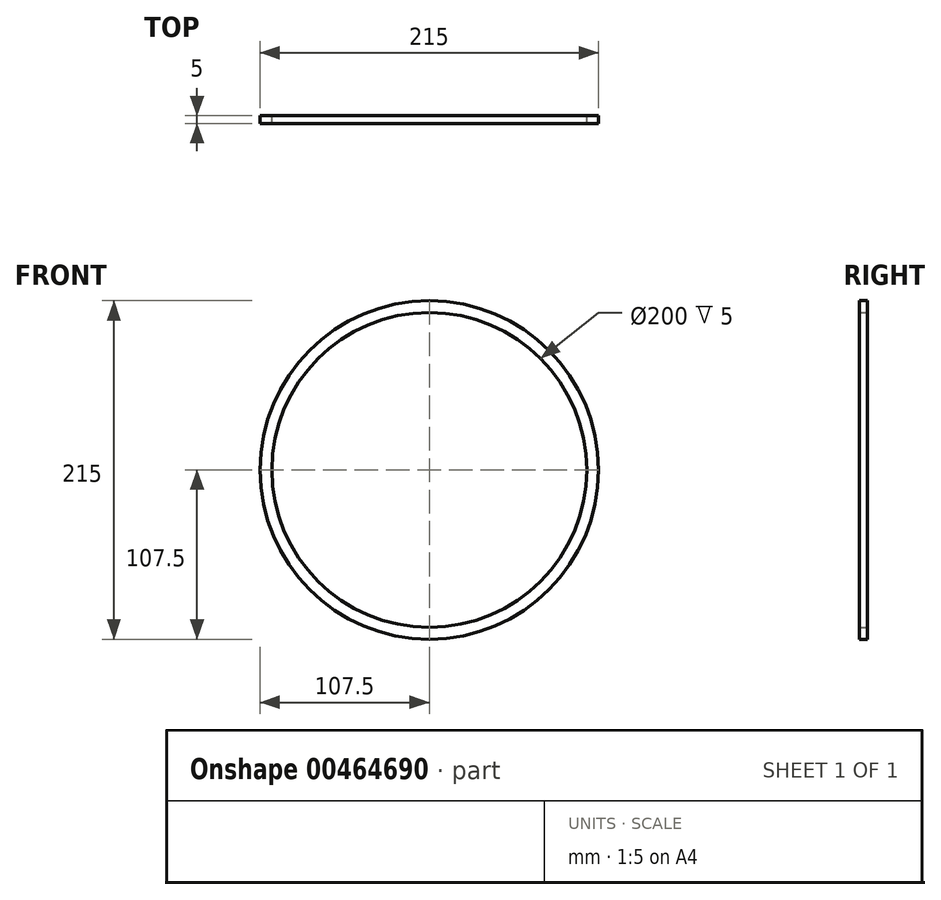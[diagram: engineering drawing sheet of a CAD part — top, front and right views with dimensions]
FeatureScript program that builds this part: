
annotation { "Feature Type Name" : "Feature", "Feature Type Description" : "" }
export const myFeature = defineFeature(function(context is Context, id is Id, definition is map)
    precondition{}
    {
        {
            var Q0;
            Q0=qCreatedBy(makeId("Front.planeOp"),FACE);
            var sketch = newSketch(context, id + "F0", { "sketchPlane" : qUnion([Q0])});
            skCircle(sketch, "E0", {"center": v(0, 0) * mm, "radius": 95 * mm, "construction": true});
            skCircle(sketch, "E1", {"center": v(0, 0) * mm, "radius": 105 * mm, "construction": true});
            skLineSegment(sketch, "E2", {"start": v(0, 0) * mm, "end": v(0, 105) * mm, "construction": true});
            skLineSegment(sketch, "E3.1.0", {"start": v(0, 0) * mm, "end": v(-67.5, 80.43) * mm, "construction": true});
            skLineSegment(sketch, "E3.2.0", {"start": v(0, 0) * mm, "end": v(-103.4, 18.23) * mm, "construction": true});
            skLineSegment(sketch, "E3.3.0", {"start": v(0, 0) * mm, "end": v(-90.93, -52.5) * mm, "construction": true});
            skLineSegment(sketch, "E3.4.0", {"start": v(0, 0) * mm, "end": v(-35.91, -98.67) * mm, "construction": true});
            skLineSegment(sketch, "E3.5.0", {"start": v(0, 0) * mm, "end": v(35.91, -98.67) * mm, "construction": true});
            skLineSegment(sketch, "E3.6.0", {"start": v(0, 0) * mm, "end": v(90.93, -52.5) * mm, "construction": true});
            skLineSegment(sketch, "E3.7.0", {"start": v(0, 0) * mm, "end": v(103.4, 18.23) * mm, "construction": true});
            skLineSegment(sketch, "E3.8.0", {"start": v(0, 0) * mm, "end": v(67.5, 80.43) * mm, "construction": true});
            skCircle(sketch, "E4", {"center": v(0, 0) * mm, "radius": 47.5 * mm, "construction": true});
            skCircle(sketch, "E5", {"center": v(0, 0) * mm, "radius": 55 * mm, "construction": true});
            skCircle(sketch, "E6", {"center": v(0, 0) * mm, "radius": 107.5 * mm});
            skCircle(sketch, "E7", {"center": v(0, 0) * mm, "radius": 100 * mm});
            skSolve(sketch);
        }
        {
            var Q0;
            Q0 = qSketchRegion(id + "F0", true);
            extrude(context, id + "F1", {"entities" : qUnion([Q0]), "depth" : 5 * mm});
        }
    });
